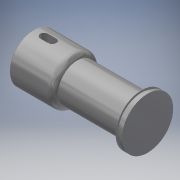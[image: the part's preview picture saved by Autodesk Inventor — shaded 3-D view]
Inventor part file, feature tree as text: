
AUTODESK INVENTOR PART (.ipt)
format: ipt  version: 2019 (Build 230136000, 136)  size: 176,128 bytes
history: native  units: mm
features: other x8, chamfer x1, fillet x1
ambient origin geometry x6: Origin, XZ Plane, XY Plane, X Axis, Y Axis, Z Axis
bodies: Body1 (feature_tree)
feature tree (10):
  other  "實體1"
  other  "迴轉1"
  chamfer  "倒角1"  [1 undecoded]
  fillet  "圓角1"  Radius=15.0mm
  other  "鍵槽1"
  other  "扣環槽1"
  other  "起始平面"
  other  "主要草圖"
  other  "iFeature3:1"
  other  "iFeature27:1"
note: 1 required parameter value undecoded (feature->parameter linkage not recoverable at this tier; creation-order binding heuristic only, values carry confidence <= 0.55)
